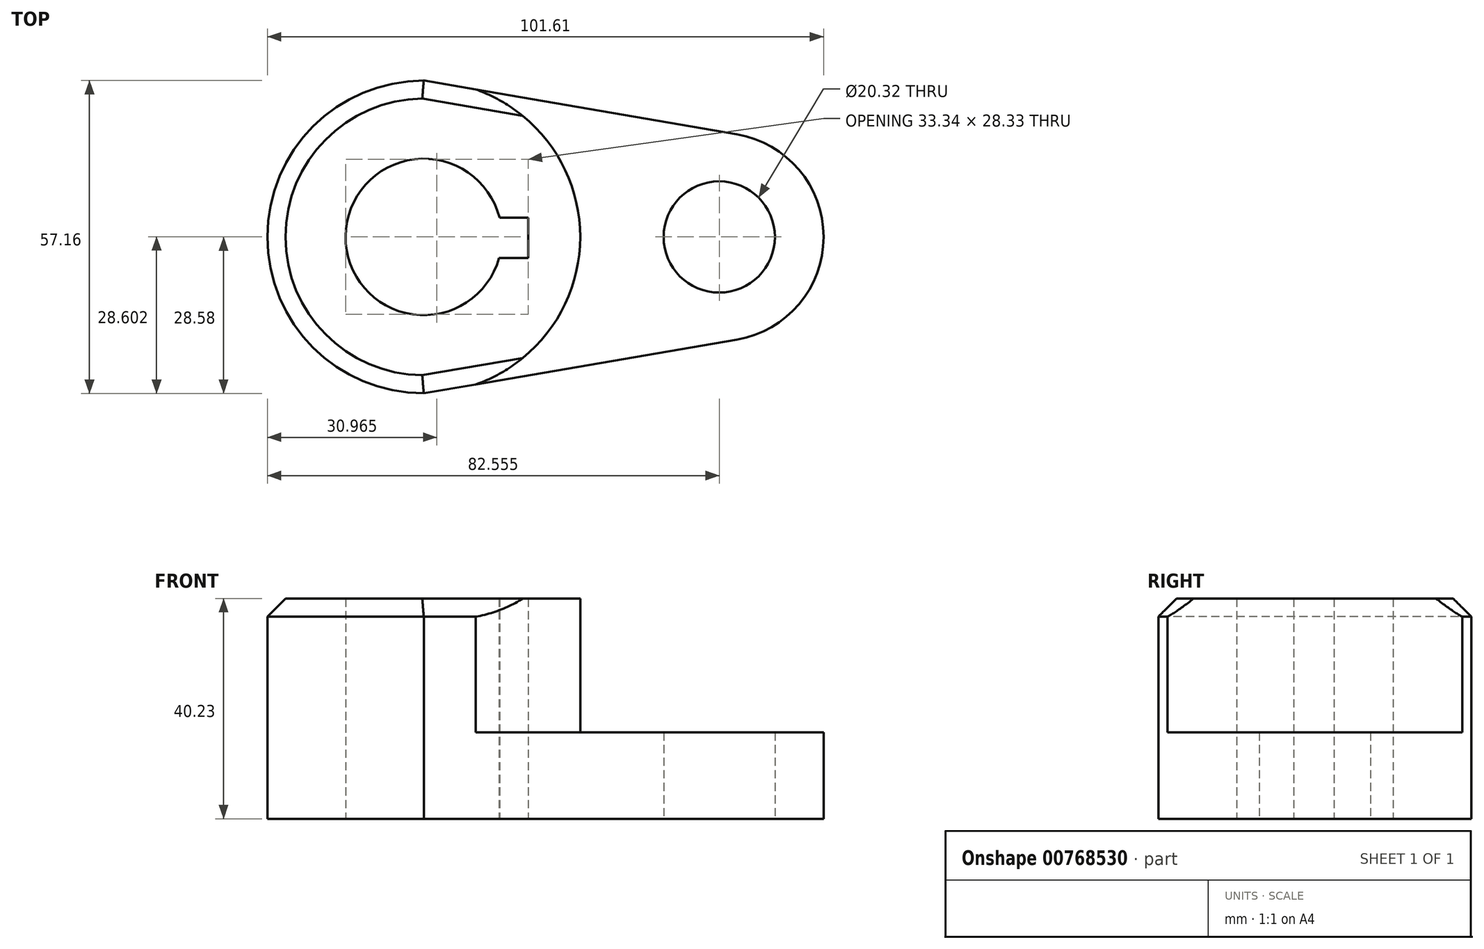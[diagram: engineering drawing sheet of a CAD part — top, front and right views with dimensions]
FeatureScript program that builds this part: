
annotation { "Feature Type Name" : "Feature", "Feature Type Description" : "" }
export const myFeature = defineFeature(function(context is Context, id is Id, definition is map)
    precondition{}
    {
        {
            var Q0;
            Q0=qCreatedBy(makeId("Top.planeOp"),FACE);
            var sketch = newSketch(context, id + "F0", { "sketchPlane" : qUnion([Q0])});
            skCircle(sketch, "E0", {"center": v(0, 0) * mm, "radius": 28.58 * mm});
            skArc(sketch, "E1", {"start": v(13.85, 3.53) * mm, "mid": v(-14.29, 0.17) * mm, "end": v(13.76, -3.85) * mm});
            skLineSegment(sketch, "E2.bottom", {"start": v(13.76, -3.85) * mm, "end": v(19.06, -3.85) * mm});
            skLineSegment(sketch, "E2.top", {"start": v(13.85, 3.53) * mm, "end": v(19.06, 3.53) * mm});
            skLineSegment(sketch, "E2.right", {"start": v(19.06, -3.85) * mm, "end": v(19.06, 3.53) * mm});
            skCircle(sketch, "E3", {"center": v(53.98, 0) * mm, "radius": 10.16 * mm});
            skArc(sketch, "E4", {"start": v(57.2, -18.78) * mm, "mid": v(73.03, 0) * mm, "end": v(57.2, 18.78) * mm});
            skLineSegment(sketch, "E5", {"start": v(0, -28.57) * mm, "end": v(57.2, -18.78) * mm});
            skLineSegment(sketch, "E6", {"start": v(0, 28.58) * mm, "end": v(57.2, 18.78) * mm});
            skSolve(sketch);
        }
        {
            var Q0;
            Q0=makeQuery(id+"F0.imprint","IMPRINT",FACE,{"disambiguationData":[TD([[makeQuery(id+"F0.imprint","IMPRINT",EDGE,{"derivedFrom":sQuery(id+"F0.wireOp",EDGE,"E3")}),-1.0]])]});
            var Q1;
            Q1=makeQuery(id+"F0.imprint","IMPRINT",FACE,{"disambiguationData":[TD([[makeQuery(id+"F0.imprint","IMPRINT",EDGE,{"derivedFrom":sQuery(id+"F0.wireOp",EDGE,"E1")}),-1.0]])]});
            extrude(context, id + "F1", {"entities" : qUnion([Q0, Q1]), "depth" : 40.23 * mm, "offsetDistance" : 25.4 * mm});
        }
        {
            var Q0;
            Q0=makeQuery(id+"F1.opExtrude","CAP_FACE",FACE,{"disambiguationData":[OSD([sQuery(id+"F0.wireOp",EDGE,"E0"),sQuery(id+"F0.wireOp",EDGE,"E1"),sQuery(id+"F0.wireOp",EDGE,"E2.bottom"),sQuery(id+"F0.wireOp",EDGE,"E2.top"),sQuery(id+"F0.wireOp",EDGE,"E2.right"),sQuery(id+"F0.wireOp",EDGE,"E3"),sQuery(id+"F0.wireOp",EDGE,"E4"),sQuery(id+"F0.wireOp",EDGE,"E5"),sQuery(id+"F0.wireOp",EDGE,"E6")])],"isStart":false});
            var sketch = newSketch(context, id + "F2", { "sketchPlane" : qUnion([Q0])});
            skCircle(sketch, "E7", {"center": v(0, 0) * mm, "radius": 28.58 * mm});
            skSolve(sketch);
        }
        {
            var Q0;
            Q0=makeQuery(id+"F2.imprint","IMPRINT",FACE,{"disambiguationData":[TD([[makeQuery(id+"F2.imprint","IMPRINT",EDGE,{"derivedFrom":makeQuery(id+"F1.opExtrude","CAP_EDGE",EDGE,{"disambiguationData":[OSD([sQuery(id+"F0.wireOp",EDGE,"E3")])],"isStart":false})}),-1.0]])]});
            extrude(context, id + "F3", {"entities" : qUnion([Q0]), "operationType" : NewBodyOperationType.REMOVE, "oppositeDirection" : true, "depth" : 24.46 * mm, "offsetDistance" : 25.4 * mm});
        }
        {
            var Q0;
            Q0=makeQuery(id+"F1.opExtrude","CAP_EDGE",EDGE,{"disambiguationData":[OSD([sQuery(id+"F0.wireOp",EDGE,"E6")])],"isStart":false});
            var Q1;
            Q1=makeQuery(id+"F3.boolean.opBoolean","COPY",EDGE,{"derivedFrom":makeQuery(id+"F3.opExtrude","CAP_EDGE",EDGE,{"disambiguationData":[OSD([sQuery(id+"F2.wireOp",EDGE,"E7")])],"isStart":true})});
            var Q2;
            Q2=makeQuery(id+"F1.opExtrude","CAP_EDGE",EDGE,{"disambiguationData":[OSD([sQuery(id+"F0.wireOp",EDGE,"E0")])],"isStart":false});
            var Q3;
            Q3=makeQuery(id+"F1.opExtrude","CAP_EDGE",EDGE,{"disambiguationData":[OSD([sQuery(id+"F0.wireOp",EDGE,"E5")])],"isStart":false});
            chamfer(context, id + "F4", {"entities" : qUnion([Q0, Q1, Q2, Q3]), "width" : 3.3 * mm, "tangentPropagation" : true});
        }
    });
